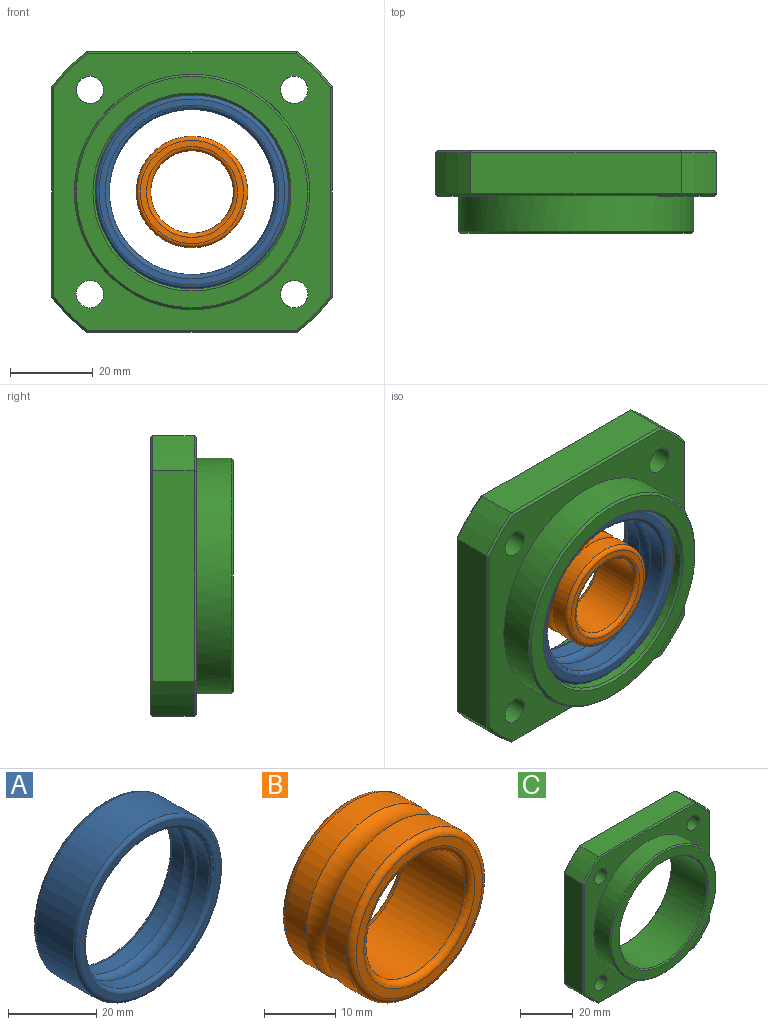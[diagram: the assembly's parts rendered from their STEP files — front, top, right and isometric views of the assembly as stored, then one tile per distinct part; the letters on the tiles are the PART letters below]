
ASSEMBLY  parts=3 mates=4
PART A: 10 faces, bbox 50.9x14x50.9 mm
  f0: torus R=22.5mm, axis (0,1,0), area 228.3mm2, adj f1,f2
  f1: plane 45x45mm, normal (0,-1,0), area 205mm2, adj f0,f9
  f2: cylinder r=23.5mm len=47mm, axis (0,-1,0), area 1771.9mm2, adj f0,f3
  f3: torus R=22.5mm, axis (0,1,0), area 228.3mm2, adj f2,f4
  f4: plane 45x45mm, normal (0,1,0), area 205mm2, adj f3,f5
  f5: torus R=21mm, axis (0,-1,0), area 201mm2, adj f4,f6
  f6: cylinder r=20mm len=40mm, axis (0,-1,0), area 518.9mm2, adj f5,f7
  f7: torus R=16.75mm, axis (0,-1,0), area 500.4mm2, adj f6,f8
  f8: cylinder r=20mm len=40mm, axis (0,-1,0), area 518.9mm2, adj f7,f9
  f9: torus R=21mm, axis (0,-1,0), area 201mm2, adj f1,f8
PART B: 10 faces, bbox 30.5x14x30.5 mm
  f0: torus R=16.75mm, axis (0,1,0), area 324.1mm2, adj f1,f2
  f1: cylinder r=13.5mm len=27mm, axis (0,-1,0), area 350.2mm2, adj f0,f9
  f2: cylinder r=13.5mm len=27mm, axis (0,-1,0), area 350.2mm2, adj f0,f3
  f3: torus R=12.5mm, axis (0,1,0), area 129.7mm2, adj f2,f4
  f4: plane 25x25mm, normal (0,1,0), area 110.7mm2, adj f3,f5
  f5: torus R=11mm, axis (0,-1,0), area 102.3mm2, adj f4,f6
  f6: cylinder r=10mm len=20mm, axis (0,-1,0), area 754mm2, adj f5,f7
  f7: torus R=11mm, axis (0,-1,0), area 102.3mm2, adj f6,f8
  f8: plane 25x25mm, normal (0,-1,0), area 110.7mm2, adj f7,f9
  f9: torus R=12.5mm, axis (0,1,0), area 129.7mm2, adj f1,f8
PART C: 43 faces, bbox 68x20x68 mm
  f0: cylinder r=5.5mm len=11mm, axis (0,1,0), area 224.6mm2, adj f1,f23
  f1: plane 11x11mm, normal (0,1,0), area 60.8mm2, adj f0,f2
  f2: cylinder r=3.3mm len=6.6mm, axis (0,1,0), area 93.3mm2, adj f1,f3
  f3: plane 67x67mm, normal (0,-1,0), area 1679.3mm2, adj f2,f4,f5,f6,f7,f26,f29,f32
  f4: plane 51x0.5mm, normal (0,-0.71,0.71), area 35.9mm2, adj f3,f5,f13,f39
  f5: cone r=42.25mm half-angle=45deg, axis (0,1,0), area 8.4mm2, adj f3,f4,f6,f14
  f6: plane 51x0.5mm, normal (0.71,-0.71,0), area 35.9mm2, adj f3,f5,f7,f15
  f7: cone r=42.25mm half-angle=45deg, axis (0,1,0), area 8.4mm2, adj f3,f6,f8,f42
  f8: cylinder r=42.5mm len=10.5mm, axis (0,1,0), area 126.2mm2, adj f7,f9,f15,f16,f22,f23
  f9: plane 51x10mm, normal (0,0,-1), area 510mm2, adj f8,f10,f22,f42
  f10: cylinder r=42.5mm len=10mm, axis (0,1,0), area 120.6mm2, adj f9,f11,f21,f41
  f11: plane 51x10mm, normal (-1,0,0), area 510mm2, adj f10,f12,f20,f40
  f12: cylinder r=42.5mm len=10mm, axis (0,1,0), area 120.6mm2, adj f11,f13,f19,f39
  f13: plane 51x10mm, normal (0,0,1), area 510mm2, adj f4,f12,f14,f18
  f14: cylinder r=42.5mm len=10mm, axis (0,1,0), area 120.6mm2, adj f5,f13,f15,f17
  f15: plane 51x10mm, normal (1,0,0), area 510mm2, adj f6,f8,f14,f16
  f16: plane 51.66x0.5mm, normal (0.71,0.71,0), area 36.2mm2, adj f8,f15,f17,f23
  f17: cone r=42.25mm half-angle=45deg, axis (0,-1,0), area 8.4mm2, adj f14,f16,f18,f23
  f18: plane 51x0.5mm, normal (0,0.71,0.71), area 35.9mm2, adj f13,f17,f19,f23
  f19: cone r=42.25mm half-angle=45deg, axis (0,-1,0), area 8.4mm2, adj f12,f18,f20,f23
  f20: plane 51x0.5mm, normal (-0.71,0.71,0), area 35.9mm2, adj f11,f19,f21,f23
  f21: cone r=42.25mm half-angle=45deg, axis (0,-1,0), area 8.4mm2, adj f10,f20,f22,f23
  f22: plane 51.66x0.5mm, normal (0,0.71,-0.71), area 36.2mm2, adj f8,f9,f21,f23
  f23: plane 67x67mm, normal (0,1,0), area 2183.7mm2, adj f0,f8,f16,f17,f18,f19,f20,f21
  f24: cylinder r=5.5mm len=11mm, axis (0,1,0), area 224.6mm2, adj f23,f25
  f25: plane 11x11mm, normal (0,1,0), area 60.8mm2, adj f24,f26
  f26: cylinder r=3.3mm len=6.6mm, axis (0,1,0), area 93.3mm2, adj f3,f25
  f27: cylinder r=5.5mm len=11mm, axis (0,1,0), area 224.6mm2, adj f23,f28
  f28: plane 11x11mm, normal (0,1,0), area 60.8mm2, adj f27,f29
  f29: cylinder r=3.3mm len=6.6mm, axis (0,1,0), area 93.3mm2, adj f3,f28
  f30: cylinder r=5.5mm len=11mm, axis (0,1,0), area 224.6mm2, adj f23,f31
  f31: plane 11x11mm, normal (0,1,0), area 60.8mm2, adj f30,f32
  f32: cylinder r=3.3mm len=6.6mm, axis (0,1,0), area 93.3mm2, adj f3,f31
  f33: cone r=23.75mm half-angle=45deg, axis (0,1,0), area 105.5mm2, adj f23,f34
  f34: cylinder r=23.5mm len=47mm, axis (0,1,0), area 2805.4mm2, adj f33,f35
  f35: cone r=23.75mm half-angle=45deg, axis (0,-1,0), area 105.5mm2, adj f34,f36
  f36: plane 56x56mm, normal (0,-1,0), area 653.5mm2, adj f35,f37
  f37: cone r=28.25mm half-angle=45deg, axis (0,1,0), area 125.5mm2, adj f36,f38
  f38: cylinder r=28.5mm len=57mm, axis (0,1,0), area 1522.1mm2, adj f3,f37
  f39: cone r=42.25mm half-angle=45deg, axis (0,1,0), area 8.4mm2, adj f3,f4,f12,f40
  f40: plane 51x0.5mm, normal (-0.71,-0.71,0), area 35.9mm2, adj f3,f11,f39,f41
  f41: cone r=42.25mm half-angle=45deg, axis (0,1,0), area 8.4mm2, adj f3,f10,f40,f42
  f42: plane 51x0.5mm, normal (0,-0.71,-0.71), area 35.9mm2, adj f3,f7,f9,f41
PLACE A rot(axis=(0,-1,0),90deg) t=(630.99,-1620.04,-201.94)mm
PLACE B rot(axis=(0.71,0,-0.71),180deg) t=(630.99,-1640.04,-201.94)mm
PLACE C rot(axis=(0,1,0),90deg) t=(630.99,-1619.04,-201.94)mm
MATE planar A.f0 <-> C.f35  axis (0,-1,0) through (630.99,-1637.04,-201.94)mm
MATE planar B.f0 <-> A.f0  axis (0,-1,0) through (630.99,-1637.04,-201.94)mm
MATE cylindrical A.f0 <-> C.f8  axis (0,-1,0) through (630.99,-1630.04,-201.94)mm
MATE slider B.f0 <-> A.f0  axis (0,1,0) through (630.99,-1626.11,-201.94)mm
